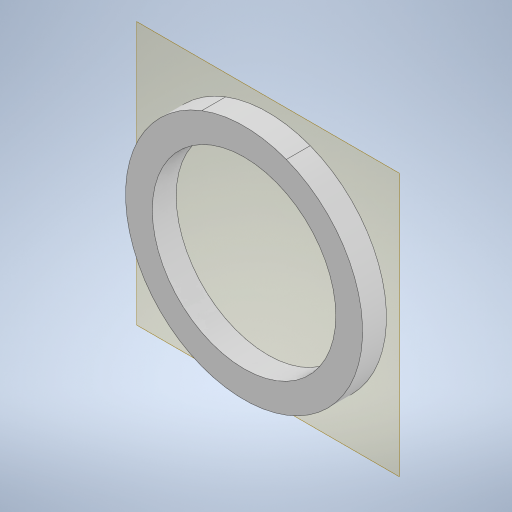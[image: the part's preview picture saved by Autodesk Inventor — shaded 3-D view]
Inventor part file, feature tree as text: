
AUTODESK INVENTOR PART (.ipt)
format: ipt  version: 2024 (Build 280153000, 153)  size: 589,824 bytes
history: native  units: mm
features: other x5, plane x3, sketch x1, extrude x1, reference x1
ambient origin geometry x8: Origin, YZ Plane, XZ Plane, XY Plane, X Axis, Y Axis, Z Axis, Center Point
bodies: Body1 (feature_tree)
feature tree (11):
  plane  "Work Plane1"
  sketch  "Sketch1"  dims[d1=0.2mm d4=0.2mm d5=0.2mm d6=10.0mm d7=0.0mm]
  plane  "Work Plane2"
  plane  "Work Plane3"
  extrude  "Extrusion2"  Depth=10.0mm
  reference  "Reference1"
  other  "<userpath>\Documents\Inventor\robot arm\arms\arms.iam"
  other  "arms.iam"
  other  "arm-bearings:2"
  other  "lower arm with pulley:1"
  other  "lower arm:1"
